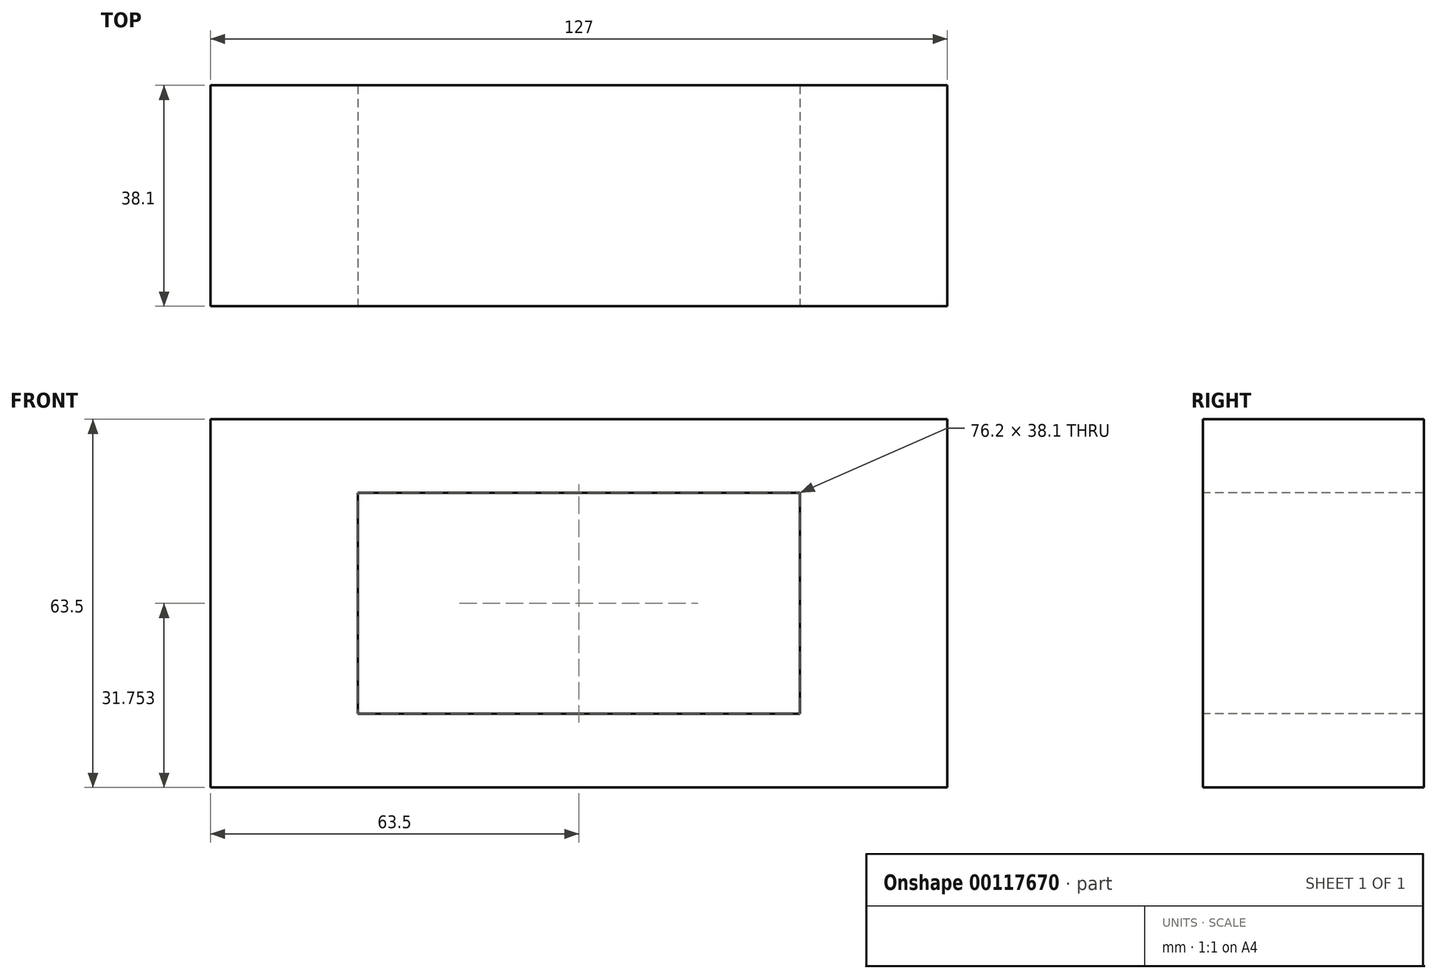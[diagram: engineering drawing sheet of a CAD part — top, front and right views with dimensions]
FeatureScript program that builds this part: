
annotation { "Feature Type Name" : "Feature", "Feature Type Description" : "" }
export const myFeature = defineFeature(function(context is Context, id is Id, definition is map)
    precondition{}
    {
        {
            var Q0;
            Q0=qCreatedBy(makeId("Right.planeOp"),FACE);
            var sketch = newSketch(context, id + "F0", { "sketchPlane" : qUnion([Q0])});
            skLineSegment(sketch, "E0.bottom", {"start": v(-44.7, 36.35) * mm, "end": v(-6.6, 36.35) * mm});
            skLineSegment(sketch, "E0.top", {"start": v(-44.7, -27.15) * mm, "end": v(-6.6, -27.15) * mm});
            skLineSegment(sketch, "E0.left", {"start": v(-44.7, 36.35) * mm, "end": v(-44.7, -27.15) * mm});
            skLineSegment(sketch, "E0.right", {"start": v(-6.6, 36.35) * mm, "end": v(-6.6, -27.15) * mm});
            skSolve(sketch);
        }
        {
            var Q0;
            Q0 = qSketchRegion(id + "F0", true);
            extrude(context, id + "F1", {"entities" : qUnion([Q0]), "oppositeDirection" : true, "depth" : 127 * mm});
        }
        {
            var Q0;
            Q0=makeQuery(id+"F1.opExtrude","SWEPT_FACE",FACE,{"disambiguationData":[OSD([sQuery(id+"F0.wireOp",EDGE,"E0.left")])]});
            var sketch = newSketch(context, id + "F2", { "sketchPlane" : qUnion([Q0])});
            skLineSegment(sketch, "E1.bottom", {"start": v(-101.6, 23.65) * mm, "end": v(-25.4, 23.65) * mm});
            skLineSegment(sketch, "E1.top", {"start": v(-101.6, -14.45) * mm, "end": v(-25.4, -14.45) * mm});
            skLineSegment(sketch, "E1.left", {"start": v(-101.6, 23.65) * mm, "end": v(-101.6, -14.45) * mm});
            skLineSegment(sketch, "E1.right", {"start": v(-25.4, 23.65) * mm, "end": v(-25.4, -14.45) * mm});
            skSolve(sketch);
        }
        {
            var Q0;
            Q0 = qSketchRegion(id + "F2", true);
            extrude(context, id + "F3", {"entities" : qUnion([Q0]), "operationType" : NewBodyOperationType.REMOVE, "endBound" : BoundingType.THROUGH_ALL, "oppositeDirection" : true, "depth" : 25.4 * mm});
        }
    });
